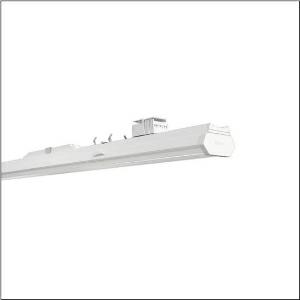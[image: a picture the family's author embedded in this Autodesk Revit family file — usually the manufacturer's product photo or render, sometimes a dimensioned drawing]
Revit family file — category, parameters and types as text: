
# Revit family: licross_r__21_protected_ho_52td11dn4axs_7332
name_source: partatom
category: Lighting Fixtures
units: mm (PartAtom-declared; Revit-internal decimal feet)

## family parameters
Cut with Voids When Loaded = No
Host = Face
Light Source = No
Part Type = Normal
Room Calculation Point = No
Round Connector Dimension = Use Diameter
Shared = No

## types (1)
- --- (1 x LED, 10000 lm, 55.1 W, 4000K)
    Apparent Load = 55 VA
    CIE Flux Codes = 84 94 98 99 100
    Color Rendering = 80
    Color Temperature = 4000K
    Default Elevation = 1800 mm
    Description = Licross® 21 Protected HO, luminaire insert, of sheet steel, galvanised, coil coated, white, length: 1.500mm, width: 90mm, height: 103mm, LED rated luminous flux: 10.000lm, light colour: 840, control gear: DALI 2, with plug, 5-pole, with phase selection, mains connection: 220..240V, AC, 50/60Hz, rated input power: 55W, halogen-free wiring, primary light control with lens, of plastic, primary optical cover: cover, of PMMA, light emission: direct distribution, primary light characteristic: symmetric, protection rating (complete): IP54, insulation class (complete): insulation class I (protective earthing), certification: CE, ENEC, VDE, UKCA, protection symbol: D if used in an environment with non-conductive dust loads with corresponding accessories, impact resistance: IK06, permissible ambient temperature for indoor applications: -25..+45°C, corresponds to IFS (International Featured Standards) requirements for safety and quality in the food industry, reducing of maximum allowable ambient temperature of 5°C with ceiling mounting, LABS conformity tested according to VDMA 24364:2018-05, packaging unit: 1 piece
    Height = 92 mm
    Lamp = 1 x LED
    Lamp Light Flux = 10000 lm
    Lamp Power = 55.1 W
    Lamp count = 1
    Length = 1500 mm
    Luminous efficacy = 181 lm/W
    Manufacturer = Siteco
    ModVariant = No
    Model = 52TD11DN4AXS
    Mounting Place = Ceiling
    Mounting Type = Pendant
    Number of Poles = 1
    OnlyDefault = Yes
    Power Factor = 1
    Product Name = Licross® 21 Protected HO
    Product group = luminaire insert
    ProductGroupID = 902
    Protection Class = Protection class I
    Protection Degree = IP 54
    RLX_Detail_Level = 1
    RLX_Emergency_Light_Flux = 0 lm
    RLX_Emergency_Type = 0
    RLX_Emergency_Type_DB = No
    RlxData = <blob elided: 24109 chars, md5=e6d05730>
    Socket = socket
    Standby Power = 0 W
    System Light Flux = 10000 lm
    System Power = 55 W
    Type Comments = factory setting: luminous flux: 100 % | dim-lin: 254 | 316 mA
    Type Image = l_1256148.jpg
    URL = http://relux.com
    VarID = @adj_128508
    Voltage = 0 V
    Weight = 0.00 kg
    Width = 88 mm

## geometry (parser evidence)
native form markers: Blend x4, Sweep x11
no freeform markers — native parametric forms only
